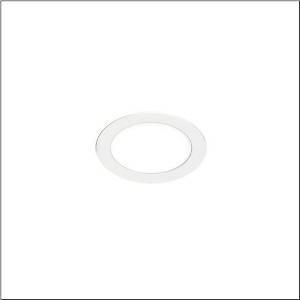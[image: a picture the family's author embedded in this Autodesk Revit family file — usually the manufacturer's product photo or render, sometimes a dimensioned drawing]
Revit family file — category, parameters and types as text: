
# Revit family: lunis_41_flat_51dr10ddgbb
name_source: partatom
category: Lighting Fixtures
units: mm (PartAtom-declared; Revit-internal decimal feet)

## family parameters
Cut with Voids When Loaded = No
Host = Face
Light Source = No
Part Type = Normal
Room Calculation Point = No
Round Connector Dimension = Use Diameter
Shared = No

## types (1)
- --- (1 x LED, 1750 lm, 14 W, 4000K)
    Apparent Load = 14 VA
    CIE Flux Codes = 49 80 96 100 100
    Color Rendering = 80
    Color Temperature = 4000K
    Default Elevation = 1800 mm
    Description = Lunis 41,  Flat, downlight, light emission: direct distribution, LED rated luminous flux: 1.575lm, light colour: 830/840, control gear: ECG, mains connection: 230V, AC, 50/60Hz, housing, round, of aluminium, coated, traffic white (RAL 9016), diameter: 170mm, protection rating (complete): IP20, protection rating (on room side): IP44, insulation class (complete): insulation class II (safety insulation), certification: CE, permissible ambient temperature for indoor applications: -20..+40°C, packaging unit: 1 piece
    Height = 0 mm  [stored 0 ft]
    Lamp = 1 x LED
    Lamp Light Flux = 1750 lm
    Lamp Power = 14 W
    Lamp count = 1
    Length = 170 mm  [stored 0.557743 ft]
    Luminous efficacy = 125 lm/W
    Manufacturer = Siteco
    ModVariant = No
    Model = 51DR10DDGBB
    Mounting Place = Ceiling
    Mounting Type = Recessed
    Number of Poles = 1
    OnlyDefault = Yes
    Power Factor = 1
    Product Name = Lunis 41 Flat
    Product group = downlight
    ProductGroupID = 400
    Protection Class = Protection class II
    Protection Degree = IP 20
    RLX_Detail_Level = 1
    RLX_Emergency_Light_Flux = 0 lm
    RLX_Emergency_Type = 0
    RLX_Emergency_Type_DB = No
    RlxData = <blob elided: 10881 chars, md5=1237a31f>
    Socket = socket
    Standby Power = 0 W
    System Light Flux = 1750 lm
    System Power = 14 W
    Type Comments = factory setting: colour temperature 4000K, luminous flux: 100 % | (ON | ON) | 350 mA
    Type Image = l_1340921.jpg
    URL = http://relux.com
    VarID = @adj_001599
    Voltage = 0 V
    Weight = 0.00 kg
    Width = 0 mm  [stored 0 ft]

note: [stored X ft] marks values corroborated as IEEE doubles in the binary element streams (Revit-internal decimal feet)

## geometry (parser evidence)
native form markers: Sweep x11
no freeform markers — native parametric forms only
